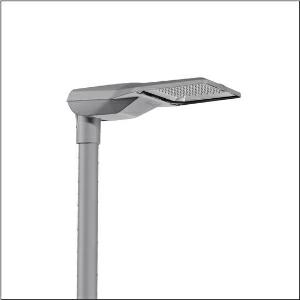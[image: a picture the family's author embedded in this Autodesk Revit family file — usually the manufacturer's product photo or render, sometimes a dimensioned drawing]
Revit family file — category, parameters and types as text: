
# Revit family: streetlight_sl_21_iq_midi___st0_8a_5xe3c61d08nb_b69d
name_source: partatom
category: Lighting Fixtures
units: mm (PartAtom-declared; Revit-internal decimal feet)

## family parameters
Cut with Voids When Loaded = No
Host = Face
Light Source = No
Part Type = Normal
Room Calculation Point = No
Round Connector Dimension = Use Diameter
Shared = No

## types (1)
- --- (1 x LED, 20820 lm, 155.5 W, 2700K)
    Apparent Load = 155 VA
    CIE Flux Codes = 41 75 97 100 100
    Color Rendering = 70
    Color Temperature = 2700K
    Default Elevation = 1800 mm
    Description = Streetlight SL 21 iQ midi, mast luminaire, primary light control with lens, of PMMA, primary optical cover: cover, of toughened safety glass, transparent, light distribution: ST0.8a, light emission: direct distribution, primary light characteristic: asymmetric, installation type: post-top, side-entry, LED, High Power LED, rated luminous flux: 20.820lm, luminous efficacy: 134lm/W, light colour: 727, colour temperature: 2700K, control: Auto-Match, Temp-Guard, Lumen-Switch, Night-Set, Smart-Wire, Light-Fading, Desk-Remote (wireless, voltage-free reading and setting of iQ features in the workshop via application-optimized NFC function/RFID function), optimised constant luminous flux control (CLO 2.0), presetting dimming linear, mains connection: 230..240V, AC, 50/60Hz, start of lifetime: 156W, end of service life: 162W, reduction: 69W, luminaire housing, of diecast aluminium, powder-coated, Siteco® metallic grey (DB 702S), corrosivity category C5 mid according to DIN EN ISO 12944, please order mast flange separately, inclination adjustable: 0°, 5°, 10°, 15°, sealing non-destructively replaceable, multi-level sealing system, length: 644mm, width: 335mm, height: 110mm, mast flange for spigot size: 42mm (side-entry): 5XC10008XM4, 60/48mm (side-entry/post-top): 5XC10108XM2, 76/60mm (side-entry/post-top): 5XC10108XM1, protection rating (complete): IP66, insulation class (complete): insulation class II (safety insulation), certification: CE, ENEC, ENEC+, VDE, impact resistance: IK09, permissible operating ambient temperature for outdoor applications: -40..+50°C, standard-compliant lighting for roads and squares, packaging unit: 1 piece

Light Distribution: ST0.8a
    Height = 111 mm
    Lamp = 1 x LED
    Lamp Light Flux = 20820 lm
    Lamp Power = 155.5 W
    Lamp count = 1
    Length = 644 mm
    Luminous efficacy = 134 lm/W
    Manufacturer = Siteco
    ModVariant = No
    Model = 5XE3C61D08NB
    Number of Poles = 1
    OnlyDefault = Yes
    Power Factor = 1
    Product Name = Streetlight SL 21 iQ midi | ST0.8a
    Product group = mast luminaire | pylon top
    ProductGroupID = 6100
    Protection Class = Protection class II
    Protection Degree = IP 66
    RLX_Detail_Level = 1
    RLX_Emergency_Light_Flux = 0 lm
    RLX_Emergency_Type = 0
    RLX_Emergency_Type_DB = No
    RlxData = <blob elided: 90905 chars, md5=b848da55>
    Socket = socket
    Standby Power = 0 W
    System Light Flux = 20820 lm
    System Power = 155 W
    Type Comments = factory setting: luminous flux: 100 % | dim-lin: 254 | 823 mA
    Type Image = l_1004298.jpg
    URL = http://relux.com
    VarID = @adj_101265
    Voltage = 0 V
    Weight = 0.00 kg
    Width = 336 mm

## geometry (parser evidence)
native form markers: Blend x4, Sweep x12
no freeform markers — native parametric forms only
